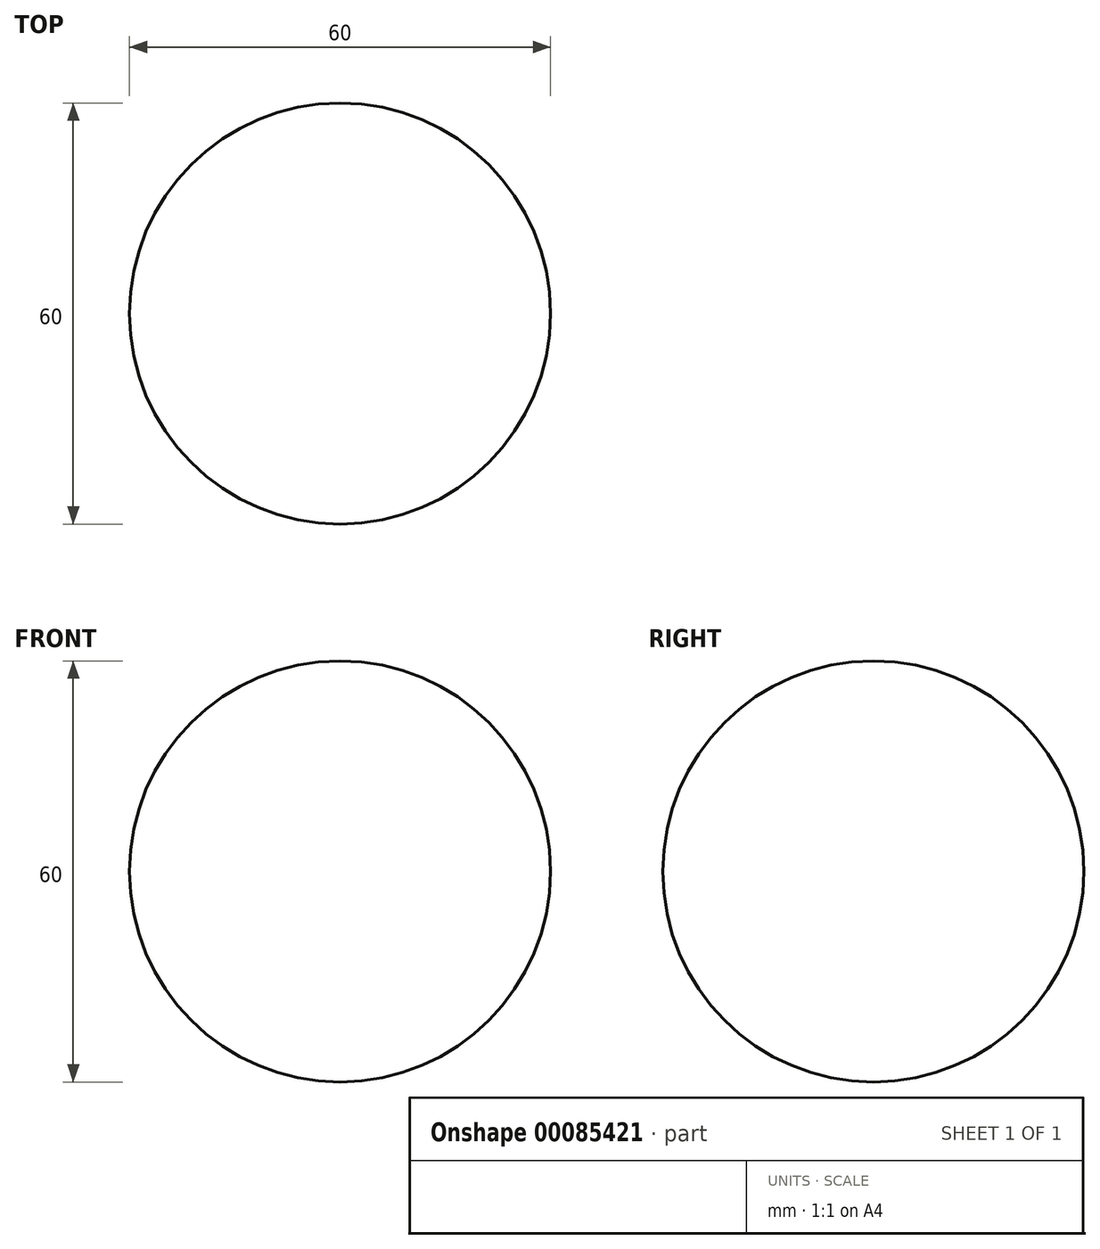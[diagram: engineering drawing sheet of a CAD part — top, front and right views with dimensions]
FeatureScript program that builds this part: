
annotation { "Feature Type Name" : "Feature", "Feature Type Description" : "" }
export const myFeature = defineFeature(function(context is Context, id is Id, definition is map)
    precondition{}
    {
        {
            var Q0;
            Q0=qCreatedBy(makeId("Front.planeOp"),FACE);
            var sketch = newSketch(context, id + "F0", { "sketchPlane" : qUnion([Q0])});
            skCircle(sketch, "E0", {"center": v(0, 0) * mm, "radius": 30 * mm});
            skSolve(sketch);
        }
        {
            var Q0;
            Q0=makeQuery(id+"F0.imprint","IMPRINT",FACE,{"disambiguationData":[TD([[makeQuery(id+"F0.imprint","IMPRINT",EDGE,{"derivedFrom":sQuery(id+"F0.wireOp",EDGE,"E0")}),1.0]])]});
            extrude(context, id + "F1", {"entities" : qUnion([Q0]), "depth" : 60 * mm});
        }
        {
            var Q0;
            Q0=makeQuery(id+"F1.opExtrude","SWEPT_FACE",FACE,{"disambiguationData":[OSD([sQuery(id+"F0.wireOp",EDGE,"E0")])]});
            var Q1;
            Q1=makeQuery(id+"F1.opExtrude","CAP_FACE",FACE,{"disambiguationData":[OSD([sQuery(id+"F0.wireOp",EDGE,"E0")])],"isStart":false});
            var Q2;
            Q2=makeQuery(id+"F1.opExtrude","CAP_FACE",FACE,{"disambiguationData":[OSD([sQuery(id+"F0.wireOp",EDGE,"E0")])],"isStart":true});
            fillet(context, id + "F2", {"entities" : qUnion([Q0, Q1, Q2]), "radius" : 30 * mm, "tangentPropagation" : true, "allowEdgeOverflow" : false});
        }
    });
